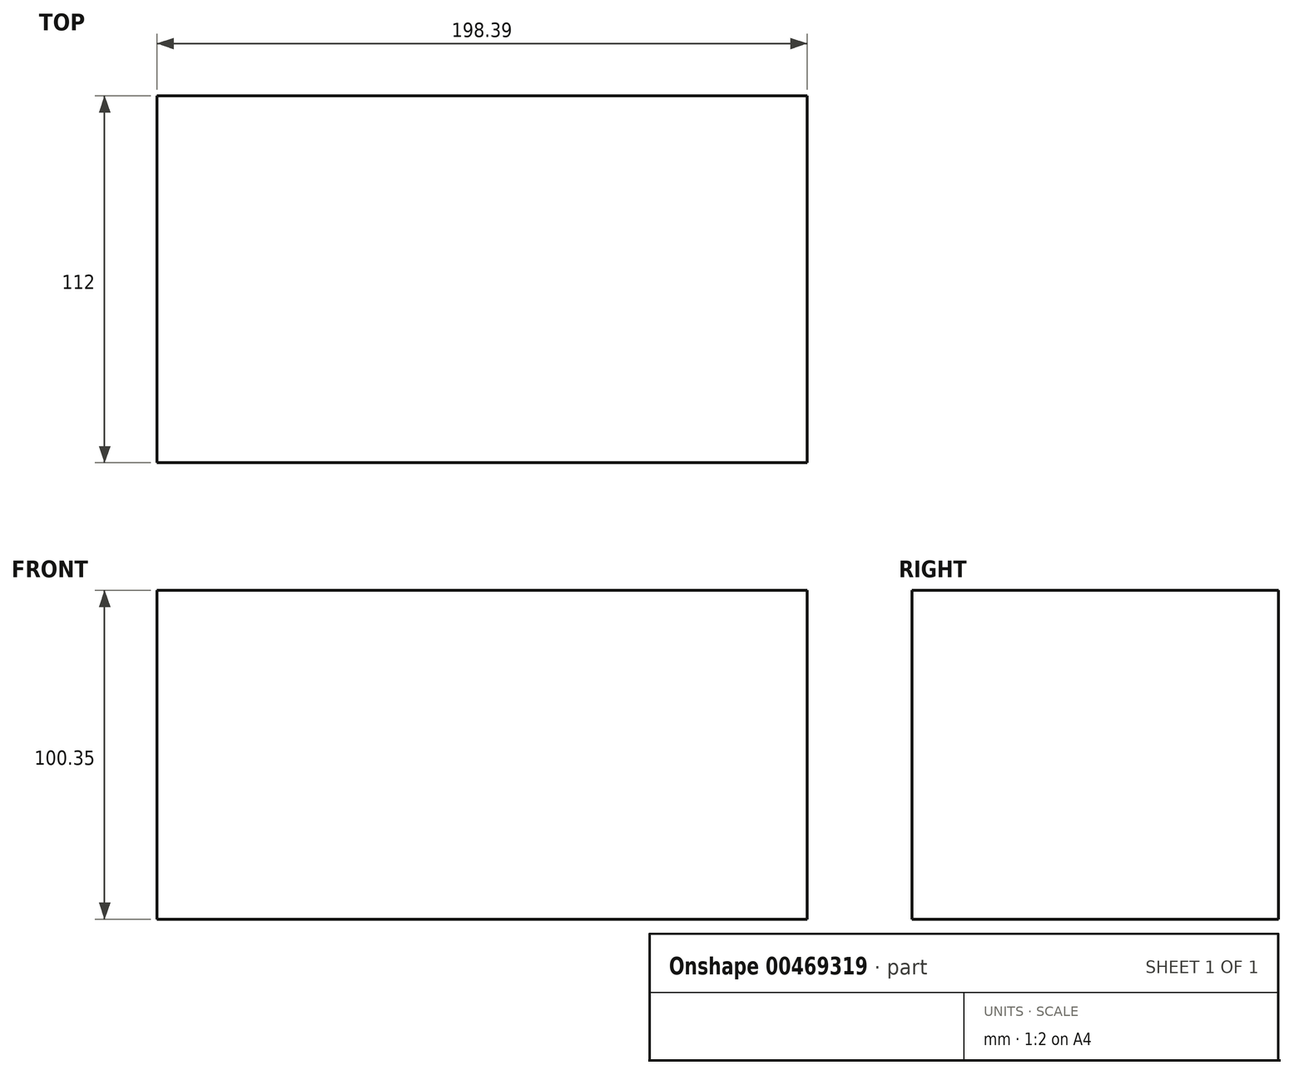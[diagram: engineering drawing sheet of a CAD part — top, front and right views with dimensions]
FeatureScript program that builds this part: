
annotation { "Feature Type Name" : "Feature", "Feature Type Description" : "" }
export const myFeature = defineFeature(function(context is Context, id is Id, definition is map)
    precondition{}
    {
        {
            var Q0;
            Q0=qCreatedBy(makeId("Front.planeOp"),FACE);
            var sketch = newSketch(context, id + "F0", { "sketchPlane" : qUnion([Q0])});
            skLineSegment(sketch, "E0.bottom", {"start": v(-261, -71.6) * mm, "end": v(-62.61, -71.6) * mm});
            skLineSegment(sketch, "E0.top", {"start": v(-261, -171.95) * mm, "end": v(-62.61, -171.95) * mm});
            skLineSegment(sketch, "E0.left", {"start": v(-261, -71.6) * mm, "end": v(-261, -171.95) * mm});
            skLineSegment(sketch, "E0.right", {"start": v(-62.61, -71.6) * mm, "end": v(-62.61, -171.95) * mm});
            skSolve(sketch);
        }
        {
            var Q0;
            Q0=makeQuery(id+"F0.imprint","IMPRINT",FACE,{"disambiguationData":[TD([[makeQuery(id+"F0.imprint","IMPRINT",EDGE,{"derivedFrom":sQuery(id+"F0.wireOp",EDGE,"E0.bottom")}),-1.0]])]});
            extrude(context, id + "F1", {"entities" : qUnion([Q0]), "oppositeDirection" : true, "depth" : 112 * mm});
        }
    });
